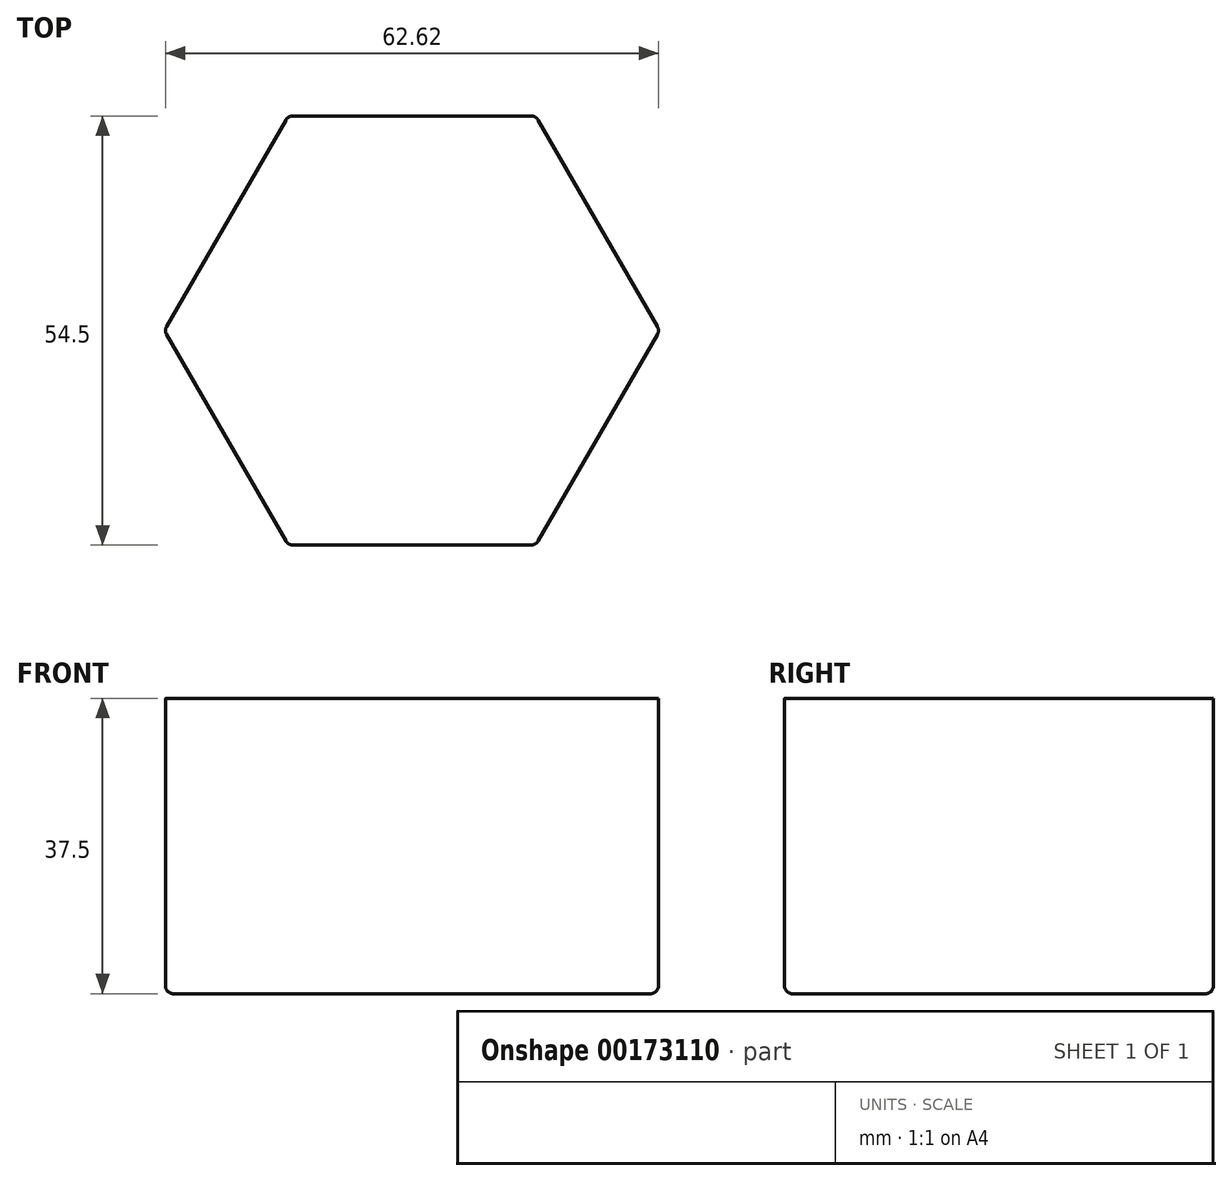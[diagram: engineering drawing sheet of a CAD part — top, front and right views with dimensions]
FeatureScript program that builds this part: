
annotation { "Feature Type Name" : "Feature", "Feature Type Description" : "" }
export const myFeature = defineFeature(function(context is Context, id is Id, definition is map)
    precondition{}
    {
        {
            var Q0;
            Q0=qCreatedBy(makeId("Top.planeOp"),FACE);
            var sketch = newSketch(context, id + "F0", { "sketchPlane" : qUnion([Q0])});
            skCircle(sketch, "E0.cCircle", {"center": v(0, 0) * mm, "radius": 27.25 * mm, "construction": true});
            skLineSegment(sketch, "E0.0", {"start": v(15.73, -27.25) * mm, "end": v(-15.73, -27.25) * mm});
            skLineSegment(sketch, "E0.1", {"start": v(-15.73, -27.25) * mm, "end": v(-31.47, 0) * mm});
            skLineSegment(sketch, "E0.2", {"start": v(-31.47, 0) * mm, "end": v(-15.73, 27.25) * mm});
            skLineSegment(sketch, "E0.3", {"start": v(-15.73, 27.25) * mm, "end": v(15.73, 27.25) * mm});
            skLineSegment(sketch, "E0.4", {"start": v(15.73, 27.25) * mm, "end": v(31.47, 0) * mm});
            skLineSegment(sketch, "E0.5", {"start": v(31.47, 0) * mm, "end": v(15.73, -27.25) * mm});
            skPoint(sketch, "E0.0.midPoint", {"position": v(0, -27.25) * mm});
            skSolve(sketch);
        }
        {
            var Q0;
            Q0=makeQuery(id+"F0.imprint","IMPRINT",FACE,{"disambiguationData":[TD([[makeQuery(id+"F0.imprint","IMPRINT",EDGE,{"derivedFrom":sQuery(id+"F0.wireOp",EDGE,"E0.0")}),-1.0]])]});
            extrude(context, id + "F1", {"entities" : qUnion([Q0]), "depth" : 37.5 * mm});
        }
        {
            var Q0;
            Q0=makeQuery(id+"F1.opExtrude","CAP_FACE",FACE,{"disambiguationData":[OSD([sQuery(id+"F0.wireOp",EDGE,"E0.0"),sQuery(id+"F0.wireOp",EDGE,"E0.1"),sQuery(id+"F0.wireOp",EDGE,"E0.2"),sQuery(id+"F0.wireOp",EDGE,"E0.3"),sQuery(id+"F0.wireOp",EDGE,"E0.4"),sQuery(id+"F0.wireOp",EDGE,"E0.5")])],"isStart":true});
            var Q1;
            Q1=makeQuery(id+"F1.opExtrude","SWEPT_EDGE",EDGE,{"disambiguationData":[OSD([sQuery(id+"F0.wireOp",EDGE,"E0.0"),sQuery(id+"F0.wireOp",EDGE,"E0.5")])]});
            var Q2;
            Q2=makeQuery(id+"F1.opExtrude","SWEPT_EDGE",EDGE,{"disambiguationData":[OSD([sQuery(id+"F0.wireOp",EDGE,"E0.4"),sQuery(id+"F0.wireOp",EDGE,"E0.5")])]});
            var Q3;
            Q3=makeQuery(id+"F1.opExtrude","SWEPT_EDGE",EDGE,{"disambiguationData":[OSD([sQuery(id+"F0.wireOp",EDGE,"E0.0"),sQuery(id+"F0.wireOp",EDGE,"E0.1")])]});
            var Q4;
            Q4=makeQuery(id+"F1.opExtrude","SWEPT_EDGE",EDGE,{"disambiguationData":[OSD([sQuery(id+"F0.wireOp",EDGE,"E0.1"),sQuery(id+"F0.wireOp",EDGE,"E0.2")])]});
            var Q5;
            Q5=makeQuery(id+"F1.opExtrude","SWEPT_EDGE",EDGE,{"disambiguationData":[OSD([sQuery(id+"F0.wireOp",EDGE,"E0.2"),sQuery(id+"F0.wireOp",EDGE,"E0.3")])]});
            var Q6;
            Q6=makeQuery(id+"F1.opExtrude","SWEPT_EDGE",EDGE,{"disambiguationData":[OSD([sQuery(id+"F0.wireOp",EDGE,"E0.3"),sQuery(id+"F0.wireOp",EDGE,"E0.4")])]});
            fillet(context, id + "F2", {"entities" : qUnion([Q0, Q1, Q2, Q3, Q4, Q5, Q6]), "radius" : 1 * mm, "tangentPropagation" : true, "allowEdgeOverflow" : false});
        }
    });
